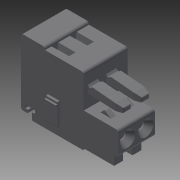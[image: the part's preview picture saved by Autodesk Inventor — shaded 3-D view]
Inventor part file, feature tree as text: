
AUTODESK INVENTOR PART (.ipt)
format: ipt  version: 2014 (Build 180170000, 170)  size: 354,304 bytes
history: native  units: mm
features: sketch x20, extrude x19, pattern_linear x6, revolve x1
ambient origin geometry x8: Origin, YZ Plane, XZ Plane, XY Plane, X Axis, Y Axis, Z Axis, Center Point
bodies: Solid1 (feature_tree)
feature tree (46):
  extrude  "Extrusion1"  Depth=1.5mm TaperAngle=0.0deg
  extrude  "Extrusion2"  Depth=1.5mm TaperAngle=0.0deg
  extrude  "Extrusion3"  Depth=1.5mm TaperAngle=0.0deg
  extrude  "Extrusion4"  Depth=1.5mm TaperAngle=0.0deg
  extrude  "Extrusion5"  TaperAngle=360.0deg  [1 undecoded]
  extrude  "Extrusion6"  Depth=3.3mm TaperAngle=0.0deg
  extrude  "Extrusion7"  Depth=1.0mm TaperAngle=0.0deg
  extrude  "Extrusion8"  Depth=1.0mm TaperAngle=0.0deg
  extrude  "Extrusion9"  Depth=0.9mm TaperAngle=0.0deg
  revolve  "Revolution1"  [1 undecoded]
  pattern_linear  "Rectangular Pattern1"  Count1=2 Spacing1=3.5mm
  extrude  "Extrusion10"  Depth=3.5mm TaperAngle=0.0deg
  pattern_linear  "Rectangular Pattern2"  [2 undecoded]
  extrude  "Extrusion11"  [1 undecoded]
  pattern_linear  "Rectangular Pattern3"  [2 undecoded]
  extrude  "Extrusion12"  [1 undecoded]
  pattern_linear  "Rectangular Pattern4"  [2 undecoded]
  extrude  "Extrusion13"  [1 undecoded]
  extrude  "Extrusion14"  [1 undecoded]
  extrude  "Extrusion15"  [1 undecoded]
  extrude  "Extrusion16"  [1 undecoded]
  extrude  "Extrusion17"  [1 undecoded]
  pattern_linear  "Rectangular Pattern5"  [2 undecoded]
  extrude  "Extrusion18"  [1 undecoded]
  pattern_linear  "Rectangular Pattern6"  [2 undecoded]
  extrude  "Extrusion19"  [1 undecoded]
  sketch  "Skizze_1"  dims[d0=7.0mm d1=0.0mm d2=1.5mm d3=0.0mm]
  sketch  "Skizze_3"  dims[d8=1.5mm d9=0.0mm d10=1.5mm d11=0.0mm]
  sketch  "Skizze_4"  dims[d12=1.5mm d13=0.0mm d14=1.5mm d15=0.0mm]
  sketch  "Skizze_5"  dims[d16=1.4mm d17=0.0mm d18=360.0deg]
  sketch  "Skizze_6"  dims[d19=20.0mm d21=3.5mm d22=10.0mm d24=0.0mm d25=3.3mm d26=0.0mm]
  sketch  "Skizze_7"  dims[d27=20.0mm d29=3.5mm d30=10.0mm d32=0.0mm d33=1.0mm d34=0.0mm]
  sketch  "Skizze_8"  dims[d35=20.0mm d37=3.5mm d38=10.0mm d40=0.0mm d41=1.0mm d42=0.0mm]
  sketch  "Skizze_9"  dims[d43=20.0mm d45=3.5mm d46=10.0mm d48=0.0mm d49=0.9mm d50=0.0mm]
  sketch  "Skizze_2"  dims[d4=1.5mm d5=0.0mm d6=1.5mm d7=0.0mm]
  sketch  "Skizze_10"  dims[d51=0.9mm d52=0.0mm d53=1.7mm d54=0.0mm]
  sketch  "Skizze_12"  dims[d55=1.7mm d56=0.0mm]
  sketch  "Skizze_14"  dims[d57=2.0mm d58=0.0mm d59=20.0mm d61=3.5mm d62=10.0mm d64=0.0mm]
  sketch  "Skizze_16"  dims[d65=1.7mm d66=0.0mm d67=20.0mm d69=3.5mm d70=10.0mm d72=0.0mm]
  sketch  "Skizze_18"  dims[d73=2.2mm d74=0.0mm]
  sketch  "Skizze_19"
  sketch  "Skizze_20"
  sketch  "Skizze_21"
  sketch  "Skizze_22"
  sketch  "Skizze_24"
  sketch  "Skizze_26"
note: 21 required parameter values undecoded (feature->parameter linkage not recoverable at this tier; creation-order binding heuristic only, values carry confidence <= 0.55)